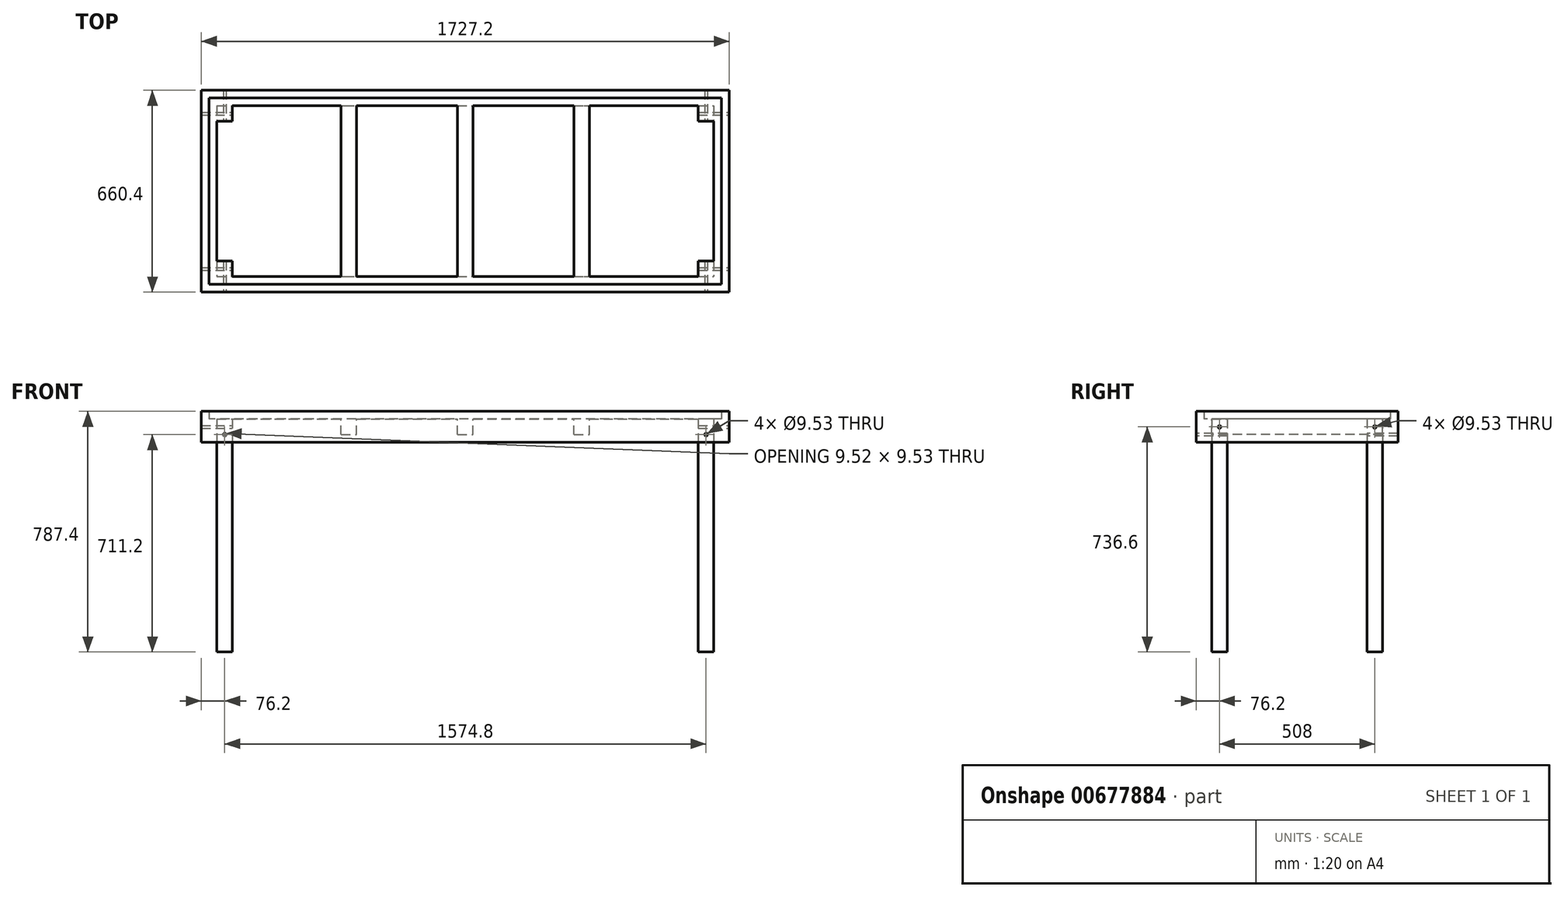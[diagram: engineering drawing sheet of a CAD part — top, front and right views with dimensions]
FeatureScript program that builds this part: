
annotation { "Feature Type Name" : "Feature", "Feature Type Description" : "" }
export const myFeature = defineFeature(function(context is Context, id is Id, definition is map)
    precondition{}
    {
        {
            var Q0;
            Q0=qCreatedBy(makeId("Top.planeOp"),FACE);
            var sketch = newSketch(context, id + "F0", { "sketchPlane" : qUnion([Q0])});
            skLineSegment(sketch, "E0.bottom", {"start": v(838.2, 304.8) * mm, "end": v(-838.2, 304.8) * mm});
            skLineSegment(sketch, "E0.top", {"start": v(838.2, -304.8) * mm, "end": v(-838.2, -304.8) * mm});
            skLineSegment(sketch, "E0.left", {"start": v(838.2, 304.8) * mm, "end": v(838.2, -304.8) * mm});
            skLineSegment(sketch, "E0.right", {"start": v(-838.2, 304.8) * mm, "end": v(-838.2, -304.8) * mm});
            skPoint(sketch, "E0.middle", {"position": v(0, 0) * mm});
            skLineSegment(sketch, "E1.bottom", {"start": v(863.6, -330.2) * mm, "end": v(-863.6, -330.2) * mm});
            skLineSegment(sketch, "E1.top", {"start": v(863.6, 330.2) * mm, "end": v(-863.6, 330.2) * mm});
            skLineSegment(sketch, "E1.left", {"start": v(863.6, -330.2) * mm, "end": v(863.6, 330.2) * mm});
            skLineSegment(sketch, "E1.right", {"start": v(-863.6, -330.2) * mm, "end": v(-863.6, 330.2) * mm});
            skSolve(sketch);
        }
        {
            var Q0;
            Q0=makeQuery(id+"F0.imprint","IMPRINT",FACE,{"disambiguationData":[TD([[makeQuery(id+"F0.imprint","IMPRINT",EDGE,{"derivedFrom":sQuery(id+"F0.wireOp",EDGE,"E0.bottom")}),-1.0]])]});
            extrude(context, id + "F1", {"entities" : qUnion([Q0]), "depth" : 101.6 * mm, "offsetDistance" : 25.4 * mm});
        }
        {
            var Q0;
            Q0=qCreatedBy(makeId("Top.planeOp"),FACE);
            var sketch = newSketch(context, id + "F2", { "sketchPlane" : qUnion([Q0])});
            skLineSegment(sketch, "E2.bottom", {"start": v(838.2, 304.8) * mm, "end": v(-838.2, 304.8) * mm});
            skLineSegment(sketch, "E2.top", {"start": v(838.2, -304.8) * mm, "end": v(-838.2, -304.8) * mm});
            skLineSegment(sketch, "E2.left", {"start": v(838.2, 304.8) * mm, "end": v(838.2, -304.8) * mm});
            skLineSegment(sketch, "E2.right", {"start": v(-838.2, 304.8) * mm, "end": v(-838.2, -304.8) * mm});
            skPoint(sketch, "E2.middle", {"position": v(0, 0) * mm});
            skLineSegment(sketch, "E3.bottom", {"start": v(-812.8, 279.4) * mm, "end": v(812.8, 279.4) * mm});
            skLineSegment(sketch, "E3.top", {"start": v(-812.8, -279.4) * mm, "end": v(812.8, -279.4) * mm});
            skLineSegment(sketch, "E3.left", {"start": v(-812.8, 279.4) * mm, "end": v(-812.8, -279.4) * mm});
            skLineSegment(sketch, "E3.right", {"start": v(812.8, 279.4) * mm, "end": v(812.8, -279.4) * mm});
            skSolve(sketch);
        }
        {
            var Q0;
            Q0=makeQuery(id+"F2.imprint","IMPRINT",FACE,{"disambiguationData":[TD([[makeQuery(id+"F2.imprint","IMPRINT",EDGE,{"derivedFrom":sQuery(id+"F2.wireOp",EDGE,"E2.bottom")}),1.0]])]});
            extrude(context, id + "F3", {"entities" : qUnion([Q0]), "operationType" : NewBodyOperationType.ADD, "depth" : 76.2 * mm, "offsetDistance" : 25.4 * mm});
        }
        {
            var Q0;
            Q0=qCreatedBy(makeId("Top.planeOp"),FACE);
            var sketch = newSketch(context, id + "F4", { "sketchPlane" : qUnion([Q0])});
            skLineSegment(sketch, "E4.bottom", {"start": v(-812.8, -279.4) * mm, "end": v(-762, -279.4) * mm});
            skLineSegment(sketch, "E4.top", {"start": v(-812.8, -228.6) * mm, "end": v(-762, -228.6) * mm});
            skLineSegment(sketch, "E4.left", {"start": v(-812.8, -279.4) * mm, "end": v(-812.8, -228.6) * mm});
            skLineSegment(sketch, "E4.right", {"start": v(-762, -279.4) * mm, "end": v(-762, -228.6) * mm});
            skLineSegment(sketch, "E5.bottom", {"start": v(-812.8, 279.4) * mm, "end": v(-762, 279.4) * mm});
            skLineSegment(sketch, "E5.top", {"start": v(-812.8, 228.6) * mm, "end": v(-762, 228.6) * mm});
            skLineSegment(sketch, "E5.left", {"start": v(-812.8, 279.4) * mm, "end": v(-812.8, 228.6) * mm});
            skLineSegment(sketch, "E5.right", {"start": v(-762, 279.4) * mm, "end": v(-762, 228.6) * mm});
            skLineSegment(sketch, "E6.bottom", {"start": v(812.8, -279.4) * mm, "end": v(762, -279.4) * mm});
            skLineSegment(sketch, "E6.top", {"start": v(812.8, -228.6) * mm, "end": v(762, -228.6) * mm});
            skLineSegment(sketch, "E6.left", {"start": v(812.8, -279.4) * mm, "end": v(812.8, -228.6) * mm});
            skLineSegment(sketch, "E6.right", {"start": v(762, -279.4) * mm, "end": v(762, -228.6) * mm});
            skLineSegment(sketch, "E7.bottom", {"start": v(812.8, 279.4) * mm, "end": v(762, 279.4) * mm});
            skLineSegment(sketch, "E7.top", {"start": v(812.8, 228.6) * mm, "end": v(762, 228.6) * mm});
            skLineSegment(sketch, "E7.left", {"start": v(812.8, 279.4) * mm, "end": v(812.8, 228.6) * mm});
            skLineSegment(sketch, "E7.right", {"start": v(762, 279.4) * mm, "end": v(762, 228.6) * mm});
            skSolve(sketch);
        }
        {
            var Q0;
            Q0 = qSketchRegion(id + "F4", true);
            extrude(context, id + "F5", {"entities" : qUnion([Q0]), "operationType" : NewBodyOperationType.ADD, "depth" : 76.2 * mm, "offsetDistance" : 25.4 * mm, "hasSecondDirection" : true, "secondDirectionOppositeDirection" : true, "secondDirectionDepth" : 685.8 * mm});
        }
        {
            var Q0;
            Q0=makeQuery(id+"F1.opExtrude","SWEPT_FACE",FACE,{"disambiguationData":[OSD([sQuery(id+"F0.wireOp",EDGE,"E1.left")])]});
            var sketch = newSketch(context, id + "F6", { "sketchPlane" : qUnion([Q0])});
            skCircle(sketch, "E8", {"center": v(-254, 50.8) * mm, "radius": 4.76 * mm});
            skCircle(sketch, "E9", {"center": v(254, 50.8) * mm, "radius": 4.76 * mm});
            skSolve(sketch);
        }
        {
            var Q0;
            Q0 = qSketchRegion(id + "F6", true);
            extrude(context, id + "F7", {"entities" : qUnion([Q0]), "operationType" : NewBodyOperationType.REMOVE, "endBound" : BoundingType.THROUGH_ALL, "oppositeDirection" : true, "depth" : 25.4 * mm, "offsetDistance" : 25.4 * mm});
        }
        {
            var Q0;
            Q0=makeQuery(id+"F1.opExtrude","SWEPT_FACE",FACE,{"disambiguationData":[OSD([sQuery(id+"F0.wireOp",EDGE,"E1.bottom")])]});
            var sketch = newSketch(context, id + "F8", { "sketchPlane" : qUnion([Q0])});
            skCircle(sketch, "E10", {"center": v(-787.4, 25.4) * mm, "radius": 4.76 * mm});
            skCircle(sketch, "E11", {"center": v(787.4, 25.4) * mm, "radius": 4.76 * mm});
            skSolve(sketch);
        }
        {
            var Q0;
            Q0 = qSketchRegion(id + "F8", true);
            extrude(context, id + "F9", {"entities" : qUnion([Q0]), "operationType" : NewBodyOperationType.REMOVE, "endBound" : BoundingType.THROUGH_ALL, "oppositeDirection" : true, "depth" : 25.4 * mm, "offsetDistance" : 25.4 * mm});
        }
        {
            var Q0;
            Q0=makeQuery(id+"F5.boolean.opBoolean","MERGE",FACE,{"derivedFrom":[makeQuery(id+"F3.opExtrude","CAP_FACE",FACE,{"disambiguationData":[OSD([sQuery(id+"F2.wireOp",EDGE,"E2.bottom"),sQuery(id+"F2.wireOp",EDGE,"E2.top"),sQuery(id+"F2.wireOp",EDGE,"E2.left"),sQuery(id+"F2.wireOp",EDGE,"E2.right"),sQuery(id+"F2.wireOp",EDGE,"E3.bottom"),sQuery(id+"F2.wireOp",EDGE,"E3.top"),sQuery(id+"F2.wireOp",EDGE,"E3.left"),sQuery(id+"F2.wireOp",EDGE,"E3.right")])],"isStart":false}),makeQuery(id+"F5.opExtrude","CAP_FACE",FACE,{"disambiguationData":[OSD([sQuery(id+"F4.wireOp",EDGE,"E4.bottom"),sQuery(id+"F4.wireOp",EDGE,"E4.top"),sQuery(id+"F4.wireOp",EDGE,"E4.left"),sQuery(id+"F4.wireOp",EDGE,"E4.right")])],"isStart":false}),makeQuery(id+"F5.opExtrude","CAP_FACE",FACE,{"disambiguationData":[OSD([sQuery(id+"F4.wireOp",EDGE,"E5.bottom"),sQuery(id+"F4.wireOp",EDGE,"E5.top"),sQuery(id+"F4.wireOp",EDGE,"E5.left"),sQuery(id+"F4.wireOp",EDGE,"E5.right")])],"isStart":false}),makeQuery(id+"F5.opExtrude","CAP_FACE",FACE,{"disambiguationData":[OSD([sQuery(id+"F4.wireOp",EDGE,"E6.bottom"),sQuery(id+"F4.wireOp",EDGE,"E6.top"),sQuery(id+"F4.wireOp",EDGE,"E6.left"),sQuery(id+"F4.wireOp",EDGE,"E6.right")])],"isStart":false}),makeQuery(id+"F5.opExtrude","CAP_FACE",FACE,{"disambiguationData":[OSD([sQuery(id+"F4.wireOp",EDGE,"E7.bottom"),sQuery(id+"F4.wireOp",EDGE,"E7.top"),sQuery(id+"F4.wireOp",EDGE,"E7.left"),sQuery(id+"F4.wireOp",EDGE,"E7.right")])],"isStart":false})]});
            var sketch = newSketch(context, id + "F10", { "sketchPlane" : qUnion([Q0])});
            skLineSegment(sketch, "E12.bottom", {"start": v(-406.4, 279.4) * mm, "end": v(-355.6, 279.4) * mm});
            skLineSegment(sketch, "E12.top", {"start": v(-406.4, -279.4) * mm, "end": v(-355.6, -279.4) * mm});
            skLineSegment(sketch, "E12.left", {"start": v(-406.4, 279.4) * mm, "end": v(-406.4, -279.4) * mm});
            skLineSegment(sketch, "E12.right", {"start": v(-355.6, 279.4) * mm, "end": v(-355.6, -279.4) * mm});
            skLineSegment(sketch, "E13.bottom", {"start": v(406.4, 279.4) * mm, "end": v(355.6, 279.4) * mm});
            skLineSegment(sketch, "E13.top", {"start": v(406.4, -279.4) * mm, "end": v(355.6, -279.4) * mm});
            skLineSegment(sketch, "E13.left", {"start": v(406.4, 279.4) * mm, "end": v(406.4, -279.4) * mm});
            skLineSegment(sketch, "E13.right", {"start": v(355.6, 279.4) * mm, "end": v(355.6, -279.4) * mm});
            skLineSegment(sketch, "E14.bottom", {"start": v(-25.4, 279.4) * mm, "end": v(25.4, 279.4) * mm});
            skLineSegment(sketch, "E14.top", {"start": v(-25.4, -279.4) * mm, "end": v(25.4, -279.4) * mm});
            skLineSegment(sketch, "E14.left", {"start": v(-25.4, 279.4) * mm, "end": v(-25.4, -279.4) * mm});
            skLineSegment(sketch, "E14.right", {"start": v(25.4, 279.4) * mm, "end": v(25.4, -279.4) * mm});
            skSolve(sketch);
        }
        {
            var Q0;
            Q0 = qSketchRegion(id + "F10", true);
            extrude(context, id + "F11", {"entities" : qUnion([Q0]), "operationType" : NewBodyOperationType.ADD, "oppositeDirection" : true, "depth" : 50.8 * mm, "offsetDistance" : 25.4 * mm});
        }
    });
